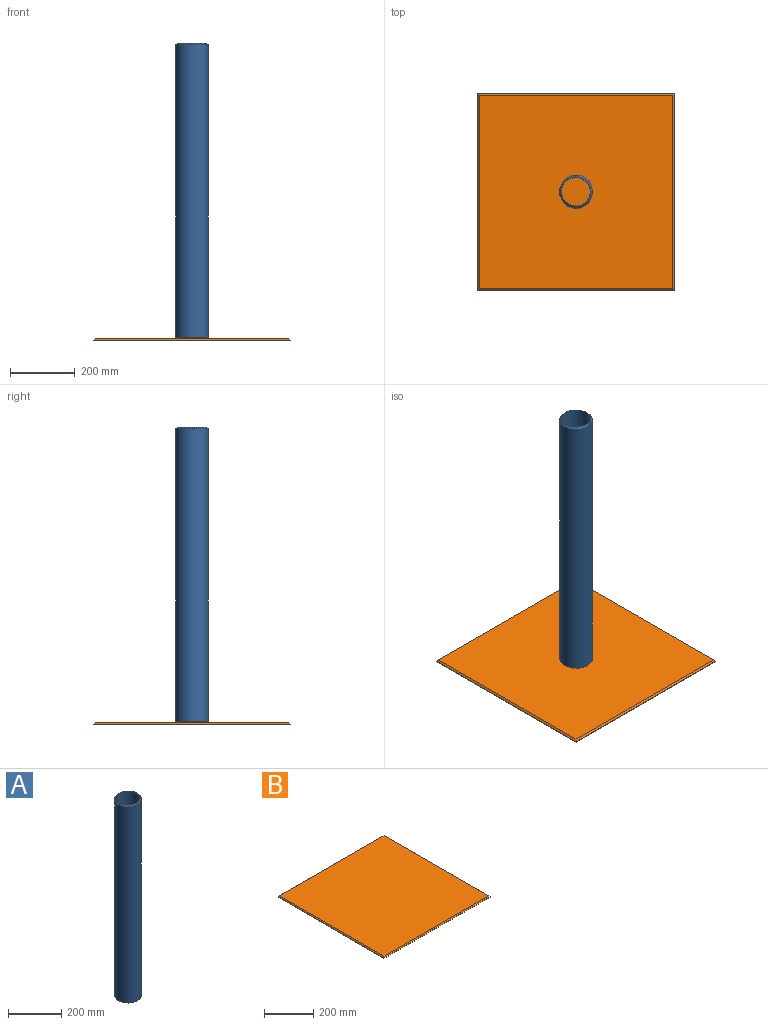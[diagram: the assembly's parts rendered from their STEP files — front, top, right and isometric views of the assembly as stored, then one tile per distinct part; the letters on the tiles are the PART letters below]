
ASSEMBLY  parts=2 mates=1
PART A: 6 faces, bbox 101.6x101.6x914.4 mm
  f0: cylinder r=44.45mm len=914.4mm, axis (0,0,1), area 255380.6mm2, adj f2,f3
  f1: cylinder r=50.8mm len=904.24mm, axis (0,0,1), area 288620.6mm2, adj f4,f5
  f2: plane 91.44x91.44mm, normal (0,0,-1), area 359.8mm2, adj f0,f5
  f3: plane 91.44x91.44mm, normal (0,0,1), area 359.8mm2, adj f0,f4
  f4: cone r=45.72mm half-angle=45deg, axis (0,0,-1), area 2178.4mm2, adj f1,f3
  f5: cone r=50.8mm half-angle=45deg, axis (0,0,1), area 2178.4mm2, adj f1,f2
PART B: 10 faces, bbox 609.6x609.6x6.4 mm
  f0: plane 609.6x1.27mm, normal (0,-1,0), area 774.2mm2, adj f1,f3,f5,f8
  f1: plane 609.6x1.27mm, normal (1,0,0), area 774.2mm2, adj f0,f2,f5,f6
  f2: plane 609.6x1.27mm, normal (0,1,0), area 774.2mm2, adj f1,f3,f5,f7
  f3: plane 609.6x1.27mm, normal (-1,0,0), area 774.2mm2, adj f0,f2,f5,f9
  f4: plane 599.44x599.44mm, normal (0,0,1), area 359328.3mm2, adj f6,f7,f8,f9
  f5: plane 609.6x609.6mm, normal (0,0,-1), area 371612.2mm2, adj f0,f1,f2,f3
  f6: plane 609.6x5.08mm, normal (0.71,0,0.71), area 4343mm2, adj f1,f4,f7,f8
  f7: plane 609.6x5.08mm, normal (0,0.71,0.71), area 4343mm2, adj f2,f4,f6,f9
  f8: plane 609.6x5.08mm, normal (0,-0.71,0.71), area 4343mm2, adj f0,f4,f6,f9
  f9: plane 609.6x5.08mm, normal (-0.71,0,0.71), area 4343mm2, adj f3,f4,f7,f8
PLACE A t=(23.65,-12.84,932.73)mm
PLACE B t=(23.65,-12.84,11.98)mm
MATE fastened A.f0 <-> B.f4  axis (0,0,-1) through (23.65,-12.84,18.33)mm
